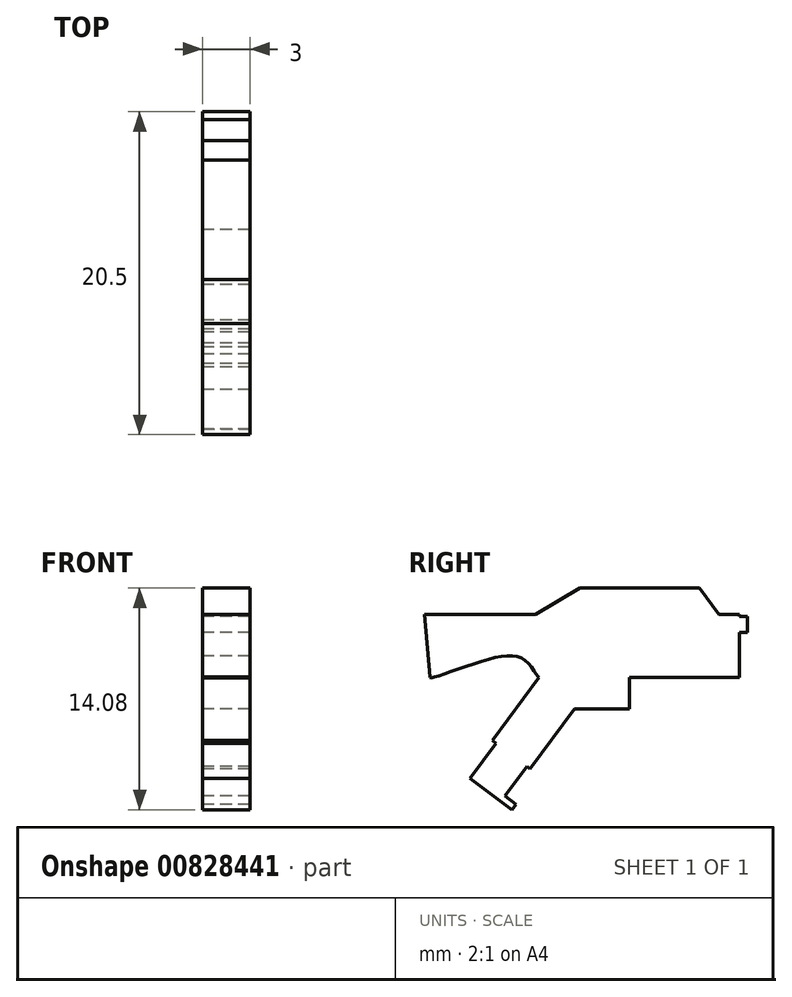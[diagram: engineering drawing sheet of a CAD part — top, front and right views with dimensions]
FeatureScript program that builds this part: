
annotation { "Feature Type Name" : "Feature", "Feature Type Description" : "" }
export const myFeature = defineFeature(function(context is Context, id is Id, definition is map)
    precondition{}
    {
        {
            var Q0;
            Q0=qCreatedBy(makeId("Right.planeOp"),FACE);
            var sketch = newSketch(context, id + "F0", { "sketchPlane" : qUnion([Q0])});
            skLineSegment(sketch, "E0", {"start": v(-4.33, 0) * mm, "end": v(-7.32, -4.01) * mm});
            skLineSegment(sketch, "E1", {"start": v(-7.32, -4.01) * mm, "end": v(-4.9, -5.8) * mm});
            skLineSegment(sketch, "E2", {"start": v(-4.9, -5.8) * mm, "end": v(-0.6, 0) * mm});
            skLineSegment(sketch, "E3", {"start": v(-11.6, 3.98) * mm, "end": v(8.4, 3.98) * mm});
            skLineSegment(sketch, "E4", {"start": v(8.4, 3.98) * mm, "end": v(8.4, 0) * mm});
            skLineSegment(sketch, "E5", {"start": v(8.4, 0) * mm, "end": v(-0.6, 0) * mm});
            skLineSegment(sketch, "E6", {"start": v(-11.6, 3.98) * mm, "end": v(-11.26, 0) * mm});
            skFitSpline(sketch, "E7", {"points": [v(-11.26, 0) * mm, v(-7.91, 1.05) * mm, v(-5.14, 1.01) * mm, v(-4.33, 0) * mm, v(-4.33, 0.62) * mm, v(-7.66, 1.69) * mm, v(-11.26, 0) * mm]});
            skLineSegment(sketch, "E8.left", {"start": v(8.4, 1.64) * mm, "end": v(8.4, 1.58) * mm});
            skLineSegment(sketch, "E9.left", {"start": v(8.4, 2.05) * mm, "end": v(8.4, 1.05) * mm});
            skLineSegment(sketch, "E10.left", {"start": v(8.4, 1.97) * mm, "end": v(8.4, 0.97) * mm});
            skLineSegment(sketch, "E11", {"start": v(8.4, 3.86) * mm, "end": v(8.9, 3.86) * mm});
            skLineSegment(sketch, "E12", {"start": v(8.9, 3.86) * mm, "end": v(8.9, 2.86) * mm});
            skLineSegment(sketch, "E13", {"start": v(8.9, 2.86) * mm, "end": v(8.4, 2.86) * mm});
            skLineSegment(sketch, "E14", {"start": v(8.75, 2.86) * mm, "end": v(8.75, -0.26) * mm});
            skLineSegment(sketch, "E15", {"start": v(8.75, -0.26) * mm, "end": v(8.4, -0.26) * mm});
            skLineSegment(sketch, "E16", {"start": v(8.4, -0.26) * mm, "end": v(8.4, 0) * mm});
            skLineSegment(sketch, "E17", {"start": v(7.08, 3.98) * mm, "end": v(5.84, 5.67) * mm});
            skLineSegment(sketch, "E18", {"start": v(5.84, 5.67) * mm, "end": v(-1.76, 5.67) * mm});
            skLineSegment(sketch, "E19", {"start": v(-1.76, 5.67) * mm, "end": v(-4.57, 3.98) * mm});
            skLineSegment(sketch, "E20", {"start": v(-4.57, 3.98) * mm, "end": v(-3.55, 3.98) * mm});
            skLineSegment(sketch, "E21", {"start": v(-3.55, 3.98) * mm, "end": v(-1.7, 5.13) * mm});
            skLineSegment(sketch, "E22", {"start": v(-1.7, 5.13) * mm, "end": v(5.28, 5.13) * mm});
            skLineSegment(sketch, "E23", {"start": v(5.28, 5.13) * mm, "end": v(6.1, 3.98) * mm});
            skLineSegment(sketch, "E24.bottom", {"start": v(2, 3.49) * mm, "end": v(3.47, 3.49) * mm});
            skLineSegment(sketch, "E24.top", {"start": v(2, 2.91) * mm, "end": v(3.47, 2.91) * mm});
            skLineSegment(sketch, "E24.left", {"start": v(2, 3.49) * mm, "end": v(2, 2.91) * mm});
            skLineSegment(sketch, "E24.right", {"start": v(3.47, 3.49) * mm, "end": v(3.47, 2.91) * mm});
            skLineSegment(sketch, "E25", {"start": v(-7.09, -4.18) * mm, "end": v(-8.74, -6.4) * mm});
            skLineSegment(sketch, "E26", {"start": v(-8.74, -6.4) * mm, "end": v(-6.06, -8.4) * mm});
            skLineSegment(sketch, "E27", {"start": v(-6.06, -8.4) * mm, "end": v(-5.8, -8.07) * mm});
            skLineSegment(sketch, "E28", {"start": v(-5.8, -8.07) * mm, "end": v(-6.5, -7.54) * mm});
            skLineSegment(sketch, "E29", {"start": v(-6.5, -7.54) * mm, "end": v(-5.21, -5.8) * mm});
            skLineSegment(sketch, "E30", {"start": v(-5.21, -5.8) * mm, "end": v(-5.1, -5.66) * mm});
            skLineSegment(sketch, "E31", {"start": v(1.4, 0) * mm, "end": v(1.4, -2.01) * mm});
            skLineSegment(sketch, "E32", {"start": v(1.4, -2.01) * mm, "end": v(-2.1, -2.01) * mm});
            skLineSegment(sketch, "E33", {"start": v(-0.6, 0) * mm, "end": v(0, -2.01) * mm});
            skLineSegment(sketch, "E34", {"start": v(0, -2.01) * mm, "end": v(0.53, -2.01) * mm});
            skLineSegment(sketch, "E35", {"start": v(0.53, -2.01) * mm, "end": v(0, 0) * mm});
            skSolve(sketch);
        }
        {
            var Q0;
            {var subQ0=sQuery(id+"F0.wireOp",EDGE,"E21");Q0=makeQuery(id+"F0.imprint","IMPRINT",FACE,{"disambiguationData":[TD([[makeQuery(id+"F0.imprint","IMPRINT",EDGE,{"derivedFrom":subQ0}),-1.0]])]});}
            var Q1;
            {var subQ0=sQuery(id+"F0.wireOp",EDGE,"E25");Q1=makeQuery(id+"F0.imprint","IMPRINT",FACE,{"disambiguationData":[TD([[makeQuery(id+"F0.imprint","IMPRINT",EDGE,{"derivedFrom":subQ0}),1.0]])]});}
            var Q2;
            {var subQ2=sQuery(id+"F0.wireOp",EDGE,"E0");Q2=makeQuery(id+"F0.imprint","IMPRINT",FACE,{"disambiguationData":[TD([[makeQuery(id+"F0.imprint","IMPRINT",EDGE,{"derivedFrom":subQ2}),1.0]])]});}
            var Q3;
            {var subQ0=sQuery(id+"F0.wireOp",EDGE,"E7");var subQ1=sQuery(id+"F0.wireOp",EDGE,"E6");var subQ2=makeQuery(id+"F0.imprint","INTERSECT",VERTEX,{"disambiguationData":[OD(0.0)],"derivedFrom":[subQ1,subQ0]});Q3=makeQuery(id+"F0.imprint","IMPRINT",FACE,{"disambiguationData":[TD([[makeQuery(id+"F0.imprint","IMPRINT",EDGE,{"disambiguationData":[TD([[subQ2,1.0]])],"derivedFrom":subQ1}),1.0]])]});}
            var Q4;
            {var subQ0=sQuery(id+"F0.wireOp",EDGE,"E17");Q4=makeQuery(id+"F0.imprint","IMPRINT",FACE,{"disambiguationData":[TD([[makeQuery(id+"F0.imprint","IMPRINT",EDGE,{"derivedFrom":subQ0}),1.0]])]});}
            var Q5;
            {var subQ0=sQuery(id+"F0.wireOp",EDGE,"E33");Q5=makeQuery(id+"F0.imprint","IMPRINT",FACE,{"disambiguationData":[TD([[makeQuery(id+"F0.imprint","IMPRINT",EDGE,{"derivedFrom":subQ0}),-1.0]])]});}
            var Q6;
            {var subQ0=sQuery(id+"F0.wireOp",EDGE,"E31");Q6=makeQuery(id+"F0.imprint","IMPRINT",FACE,{"disambiguationData":[TD([[makeQuery(id+"F0.imprint","IMPRINT",EDGE,{"derivedFrom":subQ0}),-1.0]])]});}
            var Q7;
            {var subQ0=sQuery(id+"F0.wireOp",EDGE,"E7");var subQ1=sQuery(id+"F0.wireOp",EDGE,"E6");var subQ2=makeQuery(id+"F0.imprint","INTERSECT",VERTEX,{"disambiguationData":[OD(0.0)],"derivedFrom":[subQ1,subQ0]});Q7=makeQuery(id+"F0.imprint","IMPRINT",FACE,{"disambiguationData":[TD([[makeQuery(id+"F0.imprint","IMPRINT",EDGE,{"disambiguationData":[TD([[subQ2,1.0]])],"derivedFrom":subQ1}),-1.0]])]});}
            var Q8;
            Q8=makeQuery(id+"F0.imprint","IMPRINT",FACE,{"disambiguationData":[TD([[makeQuery(id+"F0.imprint","IMPRINT",EDGE,{"derivedFrom":sQuery(id+"F0.wireOp",EDGE,"E24.bottom")}),-1.0]])]});
            var Q9;
            {var subQ0=sQuery(id+"F0.wireOp",EDGE,"E33");Q9=makeQuery(id+"F0.imprint","IMPRINT",FACE,{"disambiguationData":[TD([[makeQuery(id+"F0.imprint","IMPRINT",EDGE,{"derivedFrom":subQ0}),1.0]])]});}
            var Q10;
            {var subQ3=sQuery(id+"F0.wireOp",EDGE,"E11");Q10=makeQuery(id+"F0.imprint","IMPRINT",FACE,{"disambiguationData":[TD([[makeQuery(id+"F0.imprint","IMPRINT",EDGE,{"derivedFrom":subQ3}),-1.0]])]});}
            var Q11;
            {var subQ8=sQuery(id+"F0.wireOp",EDGE,"E9.left");Q11=makeQuery(id+"F0.imprint","IMPRINT",FACE,{"disambiguationData":[TD([[makeQuery(id+"F0.imprint","IMPRINT",EDGE,{"derivedFrom":subQ8}),1.0]])]});}
            extrude(context, id + "F1", {"entities" : qUnion([Q0, Q1, Q2, Q3, Q4, Q5, Q6, Q7, Q8, Q9, Q10, Q11]), "depth" : 3 * mm, "offsetDistance" : 25 * mm});
        }
    });
